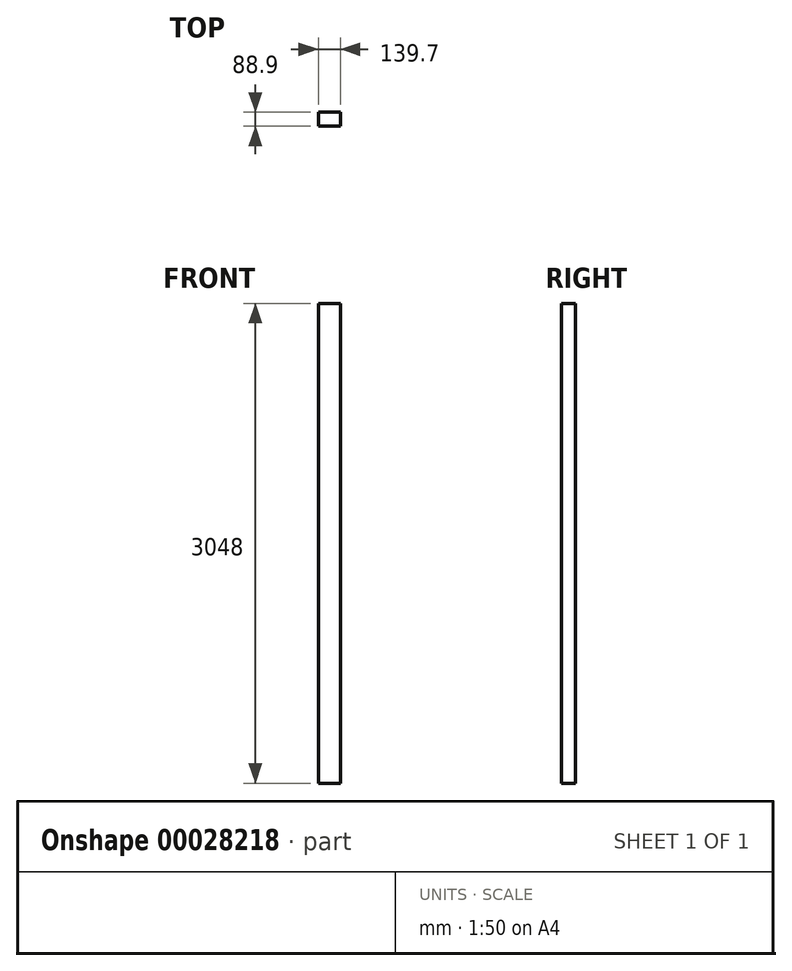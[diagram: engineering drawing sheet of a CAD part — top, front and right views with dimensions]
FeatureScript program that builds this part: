
annotation { "Feature Type Name" : "Feature", "Feature Type Description" : "" }
export const myFeature = defineFeature(function(context is Context, id is Id, definition is map)
    precondition{}
    {
        {
            var Q0;
            Q0=qCreatedBy(makeId("Top.planeOp"),FACE);
            var sketch = newSketch(context, id + "F0", { "sketchPlane" : qUnion([Q0])});
            skLineSegment(sketch, "E0.bottom", {"start": v(-80, 33.4) * mm, "end": v(59.7, 33.4) * mm});
            skLineSegment(sketch, "E0.top", {"start": v(-80, -55.5) * mm, "end": v(59.7, -55.5) * mm});
            skLineSegment(sketch, "E0.left", {"start": v(-80, 33.4) * mm, "end": v(-80, -55.5) * mm});
            skLineSegment(sketch, "E0.right", {"start": v(59.7, 33.4) * mm, "end": v(59.7, -55.5) * mm});
            skSolve(sketch);
        }
        {
            var Q0;
            Q0=makeQuery(id+"F0.imprint","IMPRINT",FACE,{"disambiguationData":[TD([[makeQuery(id+"F0.imprint","IMPRINT",EDGE,{"derivedFrom":sQuery(id+"F0.wireOp",EDGE,"E0.bottom")}),-1.0]])]});
            extrude(context, id + "F1", {"entities" : qUnion([Q0]), "depth" : 3048 * mm});
        }
    });
